# Revit family: 09_MAGIS40-33_PB1A+SERR
name_source: partatom
category: Porte
units: mm (PartAtom-declared; Revit-internal decimal feet)

## family parameters
Condiviso = No
Host = Muro
Numero OmniClass = 23.30.10.00
Punto di calcolo locali = No
Sempre verticale = Sì
Taglio con vuoti quando caricato = No
Titolo OmniClass = Doors

## types (3) — shared parameters
Chiusura muro = Per host
Codice assieme = B2030100
Costruzione analitica = <Nessuno>
EXTERNAL ALUMINUM FRAME/TELAIO ALLUMINIO ESTERNO = UNIFORM_ALUMINUM
Funzione = Interno
GLASS WEIGHT/PESO VETRO = 30.00 kg/m²
H = 2000 mm  [stored 6.56168 ft]
HANDLE HEIGHT/ALTEZZA MANIGLIA = 1100 mm
HANDLE/MANIGLIA = UNIFORM_ALUMINUM
INTERIOR WOOD FRAME/TELAIO LEGNO INTERNO = UNIFORM_WOOD
Larghezza telaio = 75 mm
MAX_DIMENSIONS_WARNING = Sì
Modello = MAGIS40
PRODUCER WEBSITE/SITO WEB PRODUTTORE = www.uniform.it
PRODUCT WEBSITE/SITO WEB PRODOTTO = www.sistema-uni-one.it
Proiezione telaio est. = 25 mm  [stored 0.082021 ft]
Proiezione telaio int. = 25 mm  [stored 0.082021 ft]
V1 = 1950 mm  [stored 6.39764 ft]
V2 = 1970 mm  [stored 6.46325 ft]
W = 1000 mm  [stored 3.28084 ft]
WINDOW GLASS/VETRO FINESTRA = UNIFORM_GLASS

## per-type parameters (varying)
| type | Altezza | Larghezza | MAXIMUM HEIGHT/ALTEZZA MASSIMA | MAXIMUM WIDTH/LARGHEZZA MASSIMA | MINIMUM HEIGHT/ALTEZZA MINIMA | MINIMUM WIDTH/LARGHEZZA MINIMA  | Rw GLASS/Rw VETRO | Rw WINDOW/Rw FINESTRA | Ug GLASS/Ug VETRO | Uw WINDOW/Uw FINESTRA |
| ACOUSTIC | 2100 mm | 1000 mm  [stored 3.28084 ft] | 2000 mm  [stored 6.56168 ft] | 1200 mm  [stored 3.93701 ft] | 400 mm  [stored 1.31234 ft] | 400 mm  [stored 1.31234 ft] | 43 | 40 | 1.6000 W/(m²·K) | 1.6000 W/(m²·K) |
| THERMAL | 2000 mm  [stored 6.56168 ft] | 1500 mm | 2500 mm | 1000 mm  [stored 3.28084 ft] | 1800 mm | 500 mm | 0 | 0 | 1.0000 W/(m²·K) | 1.4000 W/(m²·K) |
| THERMAL_PERFORMANCE | 2000 mm  [stored 6.56168 ft] | 1500 mm | 2500 mm | 1000 mm  [stored 3.28084 ft] | 1800 mm | 500 mm | 0 | 0 | 0.5000 W/(m²·K) | 1.1000 W/(m²·K) |

note: [stored X ft] marks values corroborated as IEEE doubles in the binary element streams (Revit-internal decimal feet)
